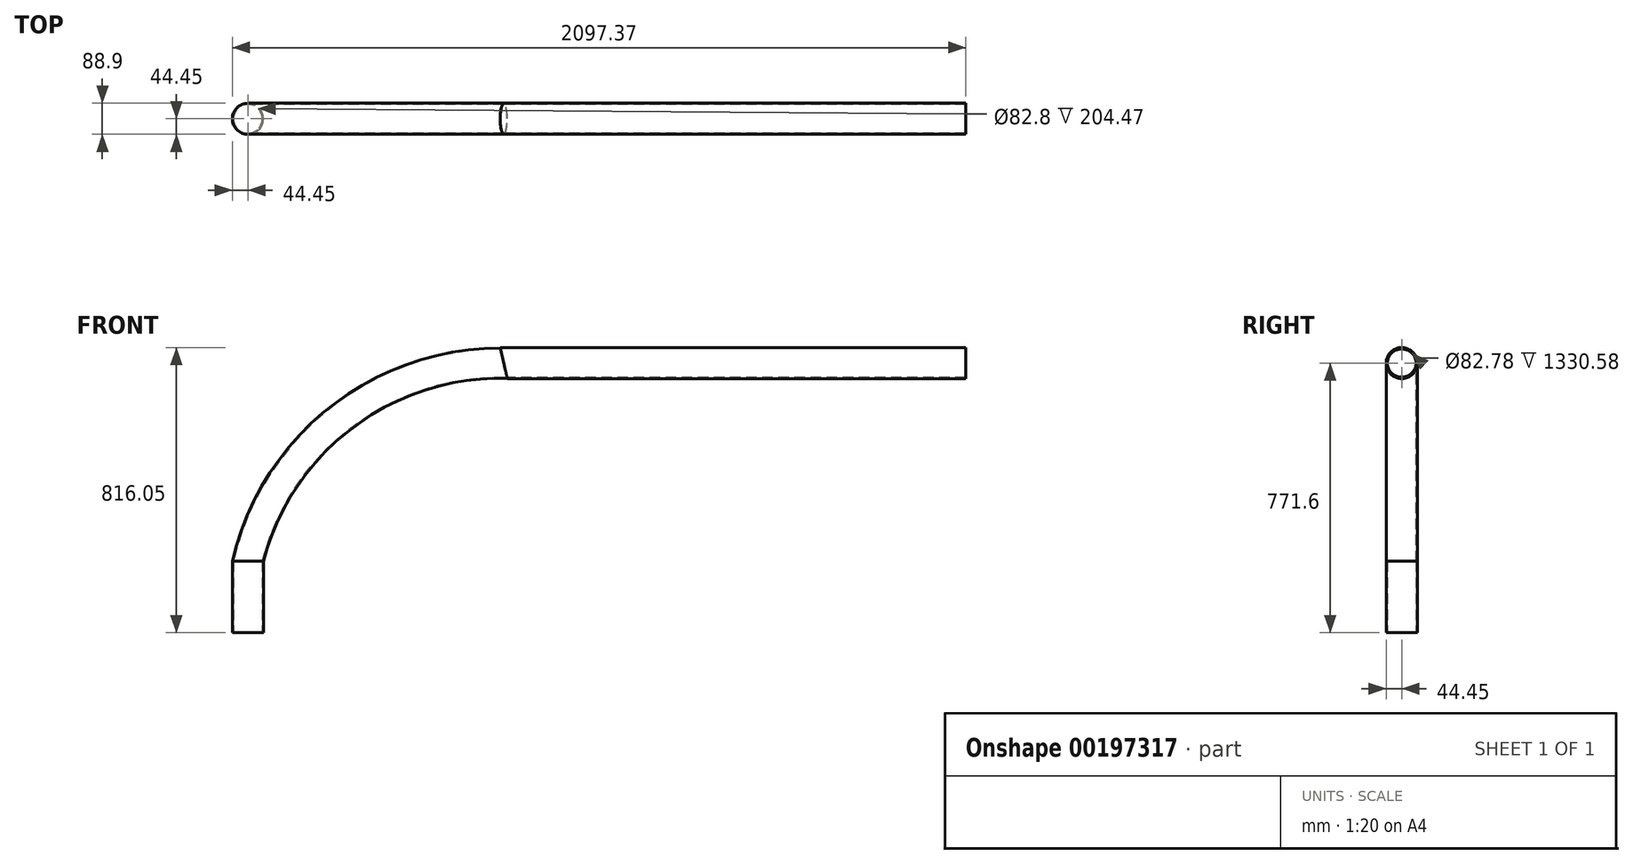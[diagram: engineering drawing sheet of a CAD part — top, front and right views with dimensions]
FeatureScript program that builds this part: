
annotation { "Feature Type Name" : "Feature", "Feature Type Description" : "" }
export const myFeature = defineFeature(function(context is Context, id is Id, definition is map)
    precondition{}
    {
        {
            var Q0;
            Q0=qCreatedBy(makeId("Top.planeOp"),FACE);
            var sketch = newSketch(context, id + "F0", { "sketchPlane" : qUnion([Q0])});
            skCircle(sketch, "E0", {"center": v(0, 0) * mm, "radius": 44.45 * mm});
            skCircle(sketch, "E1", {"center": v(0, 0) * mm, "radius": 41.4 * mm});
            skSolve(sketch);
        }
        {
            var Q0;
            Q0 = qSketchRegion(id + "F0", true);
            extrude(context, id + "F1", {"entities" : qUnion([Q0]), "depth" : 204.47 * mm});
        }
        {
            var Q0;
            Q0=makeQuery(id+"F1.opExtrude","CAP_FACE",FACE,{"disambiguationData":[OSD([sQuery(id+"F0.wireOp",EDGE,"E0"),sQuery(id+"F0.wireOp",EDGE,"E1")])],"isStart":false});
            var sketch = newSketch(context, id + "F2", { "sketchPlane" : qUnion([Q0])});
            skCircle(sketch, "E2.0", {"center": v(0, 0) * mm, "radius": 44.45 * mm});
            skCircle(sketch, "E3.0", {"center": v(0, 0) * mm, "radius": 41.4 * mm});
            skSolve(sketch);
        }
        {
            var Q0;
            Q0=qCreatedBy(makeId("Front.planeOp"),FACE);
            var sketch = newSketch(context, id + "F3", { "sketchPlane" : qUnion([Q0])});
            skLineSegment(sketch, "E4", {"start": v(54.96, 771.6) * mm, "end": v(721.96, 771.6) * mm, "construction": true});
            skPoint(sketch, "E5.visualSharp", {"position": v(4.16, 771.6) * mm});
            skArc(sketch, "E5.filletArc", {"start": v(54.96, 771.6) * mm, "mid": v(19.04, 756.72) * mm, "end": v(4.16, 720.8) * mm, "construction": true});
            skArc(sketch, "E6", {"start": v(721.96, 771.6) * mm, "mid": v(269.99, 618.37) * mm, "end": v(4.39, 221.86) * mm, "construction": true});
            skArc(sketch, "E7.0", {"start": v(721.96, 814.78) * mm, "mid": v(232.1, 643.56) * mm, "end": v(-44.45, 204.47) * mm});
            skArc(sketch, "E8.0", {"start": v(721.96, 728.42) * mm, "mid": v(293.73, 582.15) * mm, "end": v(44.45, 204.47) * mm});
            skSolve(sketch);
        }
        {
            var Q0;
            Q0=sQuery(id+"F3.wireOp",VERTEX,"E4.end");
            var Q1;
            Q1=qCreatedBy(makeId("Right.planeOp"),FACE);
            cPlane(context, id + "F4", {"entities" : qUnion([Q0, Q1]), "cplaneType" : CPlaneType.PLANE_POINT, "offset" : 25.4 * mm, "width" : 152.4 * mm, "height" : 152.4 * mm});
        }
        {
            var Q0;
            Q0=qCreatedBy(id+"F4.planeOp",FACE);
            var sketch = newSketch(context, id + "F5", { "sketchPlane" : qUnion([Q0])});
            skCircle(sketch, "E9", {"center": v(0, 771.6) * mm, "radius": 44.45 * mm});
            skCircle(sketch, "E10", {"center": v(0, 771.6) * mm, "radius": 41.39 * mm});
            skSolve(sketch);
        }
        {
            var Q0;
            Q0 = qSketchRegion(id + "F2", true);
            var Q1;
            Q1=sQuery(id+"F3.wireOp",EDGE,"E7.0");
            sweep(context, id + "F6", {"operationType" : NewBodyOperationType.ADD, "profiles" : qUnion([Q0]), "path" : qUnion([Q1])});
        }
        {
            var Q0;
            Q0 = qSketchRegion(id + "F5", true);
            var Q1;
            Q1=makeQuery(id+"F6.opSweep","CAP_FACE",FACE,{"disambiguationData":[OSD([sQuery(id+"F2.wireOp",EDGE,"E2.0"),sQuery(id+"F2.wireOp",EDGE,"E3.0"),sQuery(id+"F3.wireOp",VERTEX,"E6.start")])],"isStart":false});
            extrude(context, id + "F7", {"entities" : qUnion([Q0]), "operationType" : NewBodyOperationType.ADD, "depth" : 1706.88 * mm - 375.92 * mm, "hasSecondDirection" : true, "secondDirectionBound" : SecondDirectionBoundingType.UP_TO_SURFACE, "secondDirectionOppositeDirection" : true, "secondDirectionBoundEntityFace" : qUnion([Q1]), "secondDirectionDepth" : 25.4 * mm});
        }
    });
